# Revit family: QF_ELECTROLUXPROFESSIONAL_1L059Z_TD6-20_HP
name_source: partatom
category: Attrezzature speciali
units: mm (PartAtom-declared; Revit-internal decimal feet)

## family parameters
Basato su piano di lavoro = No
Condiviso = No
Punto di calcolo locali = No
Quota connettore circolare = Usa diametro
Sempre verticale = Sì
Taglio con vuoti quando caricato = No
Tipo di parte = Normale

## types (25) — shared parameters
Height Actual = 1771 mm  [stored 5.81037 ft]
Latent Heat Output = 0.0
Length Actual = 790 mm  [stored 2.59186 ft]
Modello = TD6-20
Produttore = Electrolux Professional
Sensible Heat Output = 0.0
URL = www.electroluxprofessional.com
zero-valued in all types: Gas KW, Prospetto di default, Steam Pounds per Hour

## per-type parameters (varying)
| type | Cycle | Depth Actual | Descrizione | Item Number | Phase | Volts | Watts | Weight |
| 9873830017 | 50 Hz | 1232 mm  [stored 4.04199 ft] | TUMBLE DRYER TD6-20 20KG SST DRUM HEAT PUMP 380-415/50/3N COMPASS PRO 6G81 SE SST DO.LEFT.INS. MB STOP | 1L0E9E | 3 | 415 V | 6500 W | 308 |
| 9873830274 | 60 Hz | 1202 mm  [stored 3.94357 ft] | TUMBLE DRYER TD6-20 20KG GALVA.DRUM HEAT PUMP 220/60/1N COMPASS PRO 6G81 EU SILVER DO.LEFT MB STOP DISCON. | 1L0H3A | 1 | 220 V | 5500 W | 243 |
| 9873830264 | 50 Hz | 1202 mm  [stored 3.94357 ft] | TUMBLE DRYER TD6-20 20KG GALVA.DRUM HEAT PUMP 380-415/50/3N COMPASS PRO 6G81 EU SILVER DO.RIGHT MB DSC STOP DISCON. | 1LSPSX | 3 | 415 V | 6500 W | 243 |
| 9873830237 | 50 Hz | 1232 mm  [stored 4.04199 ft] | TUMBLE DRYER TD6-20 20KG GALVA.DRUM HEAT PUMP 400/50/3 COMPASS PRO 6G81 EU SILVER DO.RIGHT.INS. MB DSC STOP DISCON. | 1LSPG0 | 3 | 400 V | 6500 W | 308 |
| 9873830138 | 50 Hz | 1232 mm  [stored 4.04199 ft] | TUMBLE DRYER TD6-20 20KG SST DRUM HEAT PUMP 380-415/50/3N COMPASS PRO 6G81 EU SILVER DO.LEFT MB STOP DISCON. | 1LSNBD | 3 | 415 V | 6500 W | 308 |
| 9873830287 | 50 Hz | 1202 mm  [stored 3.94357 ft] | TUMBLE DRYER TD6-20 20KG SST DRUM HEAT PUMP 200/50/1 COMPASS PRO 6L85 JP SILVER DO.RIGHT.INS. ELS-NETW. DISCON. 2.I/O | 1L0H99 | 1 | 200 V | 5500 W | 243 |
| 9873830168 | 60 Hz | 1232 mm  [stored 4.04199 ft] | TUMBLE DRYER TD6-20 20KG GALVA.DRUM HEAT PUMP 440/60/3 COMPASS PRO 6G81 EU SILVER DO.LEFT.INS. MB STOP DISCON. | 1LSNLX | 3 | 440 V | 6500 W | 308 |
| 9873830282 | 60 Hz | 1202 mm  [stored 3.94357 ft] | TUMBLE DRYER TD6-20 20KG SST DRUM HEAT PUMP 200/60/1 COMPASS PRO 6G85 JP SILVER DO.RIGHT.INS. ELS-NETW. MB DISCON. | 1L0H85 | 1 | 200 V | 5500 W | 243 |
| 9873830049 | 50 Hz | 1232 mm  [stored 4.04199 ft] | TUMBLE DRYER TD6-20 20KG GALVA.DRUM HEAT PUMP 400/50/3N COMPASS PRO 6A81 SE SILVER DO.LEFT.INS. MB STOP | 1L0EFL | 3 | 400 V | 6500 W | 308 |
| 9873830074 | 50 Hz | 1232 mm  [stored 4.04199 ft] | TUMBLE DRYER TD6-20 20KG GALVA.DRUM HEAT PUMP 400/50/3 COMPASS PRO 6L80 EU SILVER DO.RIGHT EXT.PM. DISCON. 2.I/O | 1L80DX | 3 | 400 V | 6500 W | 308 |
| 9873830142 | 50 Hz | 1232 mm  [stored 4.04199 ft] | TUMBLE DRYER TD6-20 20KG SST DRUM HEAT PUMP 380-415/50/3N COMPASS PRO 6G81 EU SILVER DO.RIGHT MB STOP DISCON. | 1LSND1 | 3 | 415 V | 6500 W | 308 |
| 9873830295 | 50 Hz | 1202 mm  [stored 3.94357 ft] | TUMBLE DRYER TD6-20 20KG SST DRUM HEAT PUMP 380-415/50/3N COMPASS PRO 6G81 EU SST DO.LEFT.INS. MB STOP DISCON. | 1LA263 | 3 | 415 V | 6500 W | 243 |
| 9873830107 | 50 Hz | 1232 mm  [stored 4.04199 ft] | TUMBLE DRYER TD6-20 20KG GALVA.DRUM HEAT PUMP 380-415/50/3N COMPASS PRO 6G81 EU SILVER DO.RIGHT MB STOP DISCON. | 1L80HA | 3 | 415 V | 6500 W | 308 |
| 9873830157 | 50 Hz | 1232 mm  [stored 4.04199 ft] | TUMBLE DRYER TD6-20 20KG SST DRUM HEAT PUMP 380-415/50/3N COMPASS PRO 6G81 EU SILVER DO.RIGHT.INS. MB STOP DISCON. | 1L0FW4 | 3 | 415 V | 6500 W | 308 |
| 9873830016 | 50 Hz | 1232 mm  [stored 4.04199 ft] | TUMBLE DRYER TD6-20 20KG GALVA.DRUM HEAT PUMP 220-240/50/1N COMPASS PRO 6G81 EU SILVER DO.RIGHT.INS. MB STOP DISCON. | 1L0E9D | 1 | 240 V | 5500 W | 308 |
| 9873830263 | 50 Hz | 1202 mm  [stored 3.94357 ft] | TUMBLE DRYER TD6-20 20KG GALVA.DRUM HEAT PUMP 380-415/50/3N COMPASS PRO 6G81 EU SILVER DO.RIGHT.INS. MB DSC STOP DISCON. | 1L0H2D | 3 | 415 V | 6500 W | 243 |
| 9873830174 | 50 Hz | 1232 mm  [stored 4.04199 ft] | TUMBLE DRYER TD6-20 20KG GALVA.DRUM HEAT PUMP 220-240/50/1N COMPASS PRO 6L80 EU SILVER DO.LEFT EXT.PM. DISCON. 2.I/O | 1L0FZB | 1 | 240 V | 5500 W | 308 |
| 9873830095 | 60 Hz | 1232 mm  [stored 4.04199 ft] | TUMBLE DRYER TD6-20 20KG GALVA.DRUM HEAT PUMP 400/60/3 COMPASS PRO 6G81 EU SILVER DO.RIGHT MB STOP DISCON. | 1L80FK | 3 | 400 V | 6500 W | 308 |
| 9873830261 | 50 Hz | 1202 mm  [stored 3.94357 ft] | TUMBLE DRYER TD6-20 20KG SST DRUM HEAT PUMP 400/50/3 COMPASS PRO 6G81 EU SILVER DO.RIGHT.INS. MB DSC STOP DISCON. | 1LSPRV | 3 | 400 V | 6500 W | 243 |
| 9873830291 | 60 Hz | 1202 mm  [stored 3.94357 ft] | TUMBLE DRYER TD6-20 20KG SST DRUM HEAT PUMP 200/60/1 COMPASS PRO 6L85 JP SILVER DO.RIGHT.INS. ELS-NETW. DISCON. 2.I/O | 1L0HAD | 1 | 200 V | 5500 W | 243 |
| 9873830281 | 50 Hz | 1202 mm  [stored 3.94357 ft] | TUMBLE DRYER TD6-20 20KG SST DRUM HEAT PUMP 200/50/1 COMPASS PRO 6G85 JP SILVER DO.RIGHT.INS. ELS-NETW. MB DISCON. | 1L0H84 | 1 | 200 V | 5500 W | 243 |
| 9873830106 | 50 Hz | 1232 mm  [stored 4.04199 ft] | TUMBLE DRYER TD6-20 20KG GALVA.DRUM HEAT PUMP 380-415/50/3N COMPASS PRO 6L80 EU SILVER DO.LEFT EXT.PM. DISCON. 2.I/O | 1L80GY | 3 | 415 V | 6500 W | 308 |
| 9873830018 | 50 Hz | 1232 mm  [stored 4.04199 ft] | TUMBLE DRYER TD6-20 20KG GALVA.DRUM HEAT PUMP 380-415/50/3N COMPASS PRO 6G81 EU SILVER DO.RIGHT.INS. MB STOP DISCON. | 1L0E9F | 3 | 415 V | 6500 W | 308 |
| 9873830209 | 50 Hz | 1232 mm  [stored 4.04199 ft] | TUMBLE DRYER TD6-20 20KG GALVA.DRUM HEAT PUMP 380-415/50/3N COMPASS PRO 6G81 EU SILVER DO.RIGHT MB STOP DISCON. | 1L0GB5 | 3 | 415 V | 6500 W | 308 |
| 9873830196 | 50 Hz | 1232 mm  [stored 4.04199 ft] | TUMBLE DRYER TD6-20 20KG GALVA.DRUM HEAT PUMP 220-240/50/1N COMPASS PRO 6G81 EU SILVER DO.LEFT MB STOP DISCON. | 1LSNZ8 | 1 | 240 V | 5500 W | 308 |

note: [stored X ft] marks values corroborated as IEEE doubles in the binary element streams (Revit-internal decimal feet)

## geometry (parser evidence)
native form markers: Blend x14
no freeform markers — native parametric forms only
